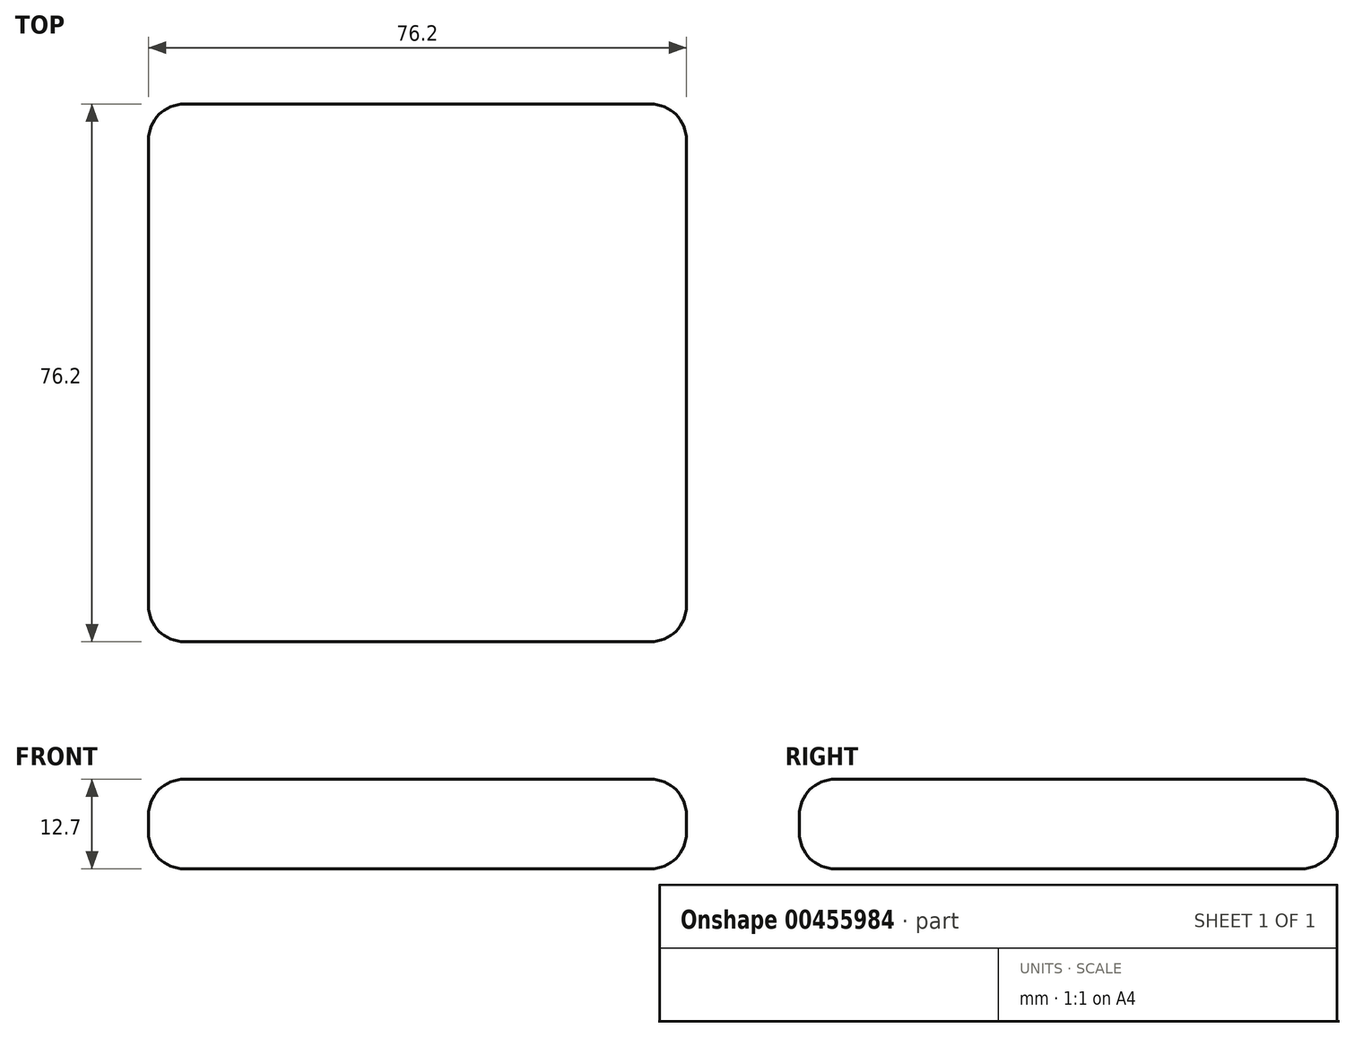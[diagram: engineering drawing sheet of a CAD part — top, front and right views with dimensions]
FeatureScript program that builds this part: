
annotation { "Feature Type Name" : "Feature", "Feature Type Description" : "" }
export const myFeature = defineFeature(function(context is Context, id is Id, definition is map)
    precondition{}
    {
        {
            var Q0;
            Q0=qCreatedBy(makeId("Top.planeOp"),FACE);
            var sketch = newSketch(context, id + "F0", { "sketchPlane" : qUnion([Q0])});
            skLineSegment(sketch, "E0.bottom", {"start": v(-38.1, 38.1) * mm, "end": v(38.1, 38.1) * mm});
            skLineSegment(sketch, "E0.top", {"start": v(-38.1, -38.1) * mm, "end": v(38.1, -38.1) * mm});
            skLineSegment(sketch, "E0.left", {"start": v(-38.1, 38.1) * mm, "end": v(-38.1, -38.1) * mm});
            skLineSegment(sketch, "E0.right", {"start": v(38.1, 38.1) * mm, "end": v(38.1, -38.1) * mm});
            skPoint(sketch, "E0.middle", {"position": v(0, 0) * mm});
            skSolve(sketch);
        }
        {
            var Q0;
            Q0 = qSketchRegion(id + "F0", true);
            extrude(context, id + "F1", {"entities" : qUnion([Q0]), "depth" : 12.7 * mm});
        }
        {
            var Q0;
            Q0=makeQuery(id+"F1.opExtrude","SWEPT_FACE",FACE,{"disambiguationData":[OSD([sQuery(id+"F0.wireOp",EDGE,"E0.top")])]});
            var Q1;
            Q1=makeQuery(id+"F1.opExtrude","CAP_EDGE",EDGE,{"disambiguationData":[OSD([sQuery(id+"F0.wireOp",EDGE,"E0.right")])],"isStart":false});
            var Q2;
            Q2=makeQuery(id+"F1.opExtrude","CAP_FACE",FACE,{"disambiguationData":[OSD([sQuery(id+"F0.wireOp",EDGE,"E0.bottom"),sQuery(id+"F0.wireOp",EDGE,"E0.top"),sQuery(id+"F0.wireOp",EDGE,"E0.left"),sQuery(id+"F0.wireOp",EDGE,"E0.right")])],"isStart":false});
            var Q3;
            Q3=makeQuery(id+"F1.opExtrude","CAP_EDGE",EDGE,{"disambiguationData":[OSD([sQuery(id+"F0.wireOp",EDGE,"E0.left")])],"isStart":false});
            var Q4;
            Q4=makeQuery(id+"F1.opExtrude","CAP_EDGE",EDGE,{"disambiguationData":[OSD([sQuery(id+"F0.wireOp",EDGE,"E0.bottom")])],"isStart":false});
            var Q5;
            Q5=makeQuery(id+"F1.opExtrude","SWEPT_FACE",FACE,{"disambiguationData":[OSD([sQuery(id+"F0.wireOp",EDGE,"E0.left")])]});
            var Q6;
            Q6=makeQuery(id+"F1.opExtrude","SWEPT_FACE",FACE,{"disambiguationData":[OSD([sQuery(id+"F0.wireOp",EDGE,"E0.bottom")])]});
            var Q7;
            Q7=makeQuery(id+"F1.opExtrude","SWEPT_FACE",FACE,{"disambiguationData":[OSD([sQuery(id+"F0.wireOp",EDGE,"E0.right")])]});
            var Q8;
            Q8=makeQuery(id+"F1.opExtrude","CAP_FACE",FACE,{"disambiguationData":[OSD([sQuery(id+"F0.wireOp",EDGE,"E0.bottom"),sQuery(id+"F0.wireOp",EDGE,"E0.top"),sQuery(id+"F0.wireOp",EDGE,"E0.left"),sQuery(id+"F0.wireOp",EDGE,"E0.right")])],"isStart":true});
            fillet(context, id + "F2", {"entities" : qUnion([Q0, Q1, Q2, Q3, Q4, Q5, Q6, Q7, Q8]), "radius" : 5.08 * mm, "tangentPropagation" : true, "allowEdgeOverflow" : false});
        }
    });
